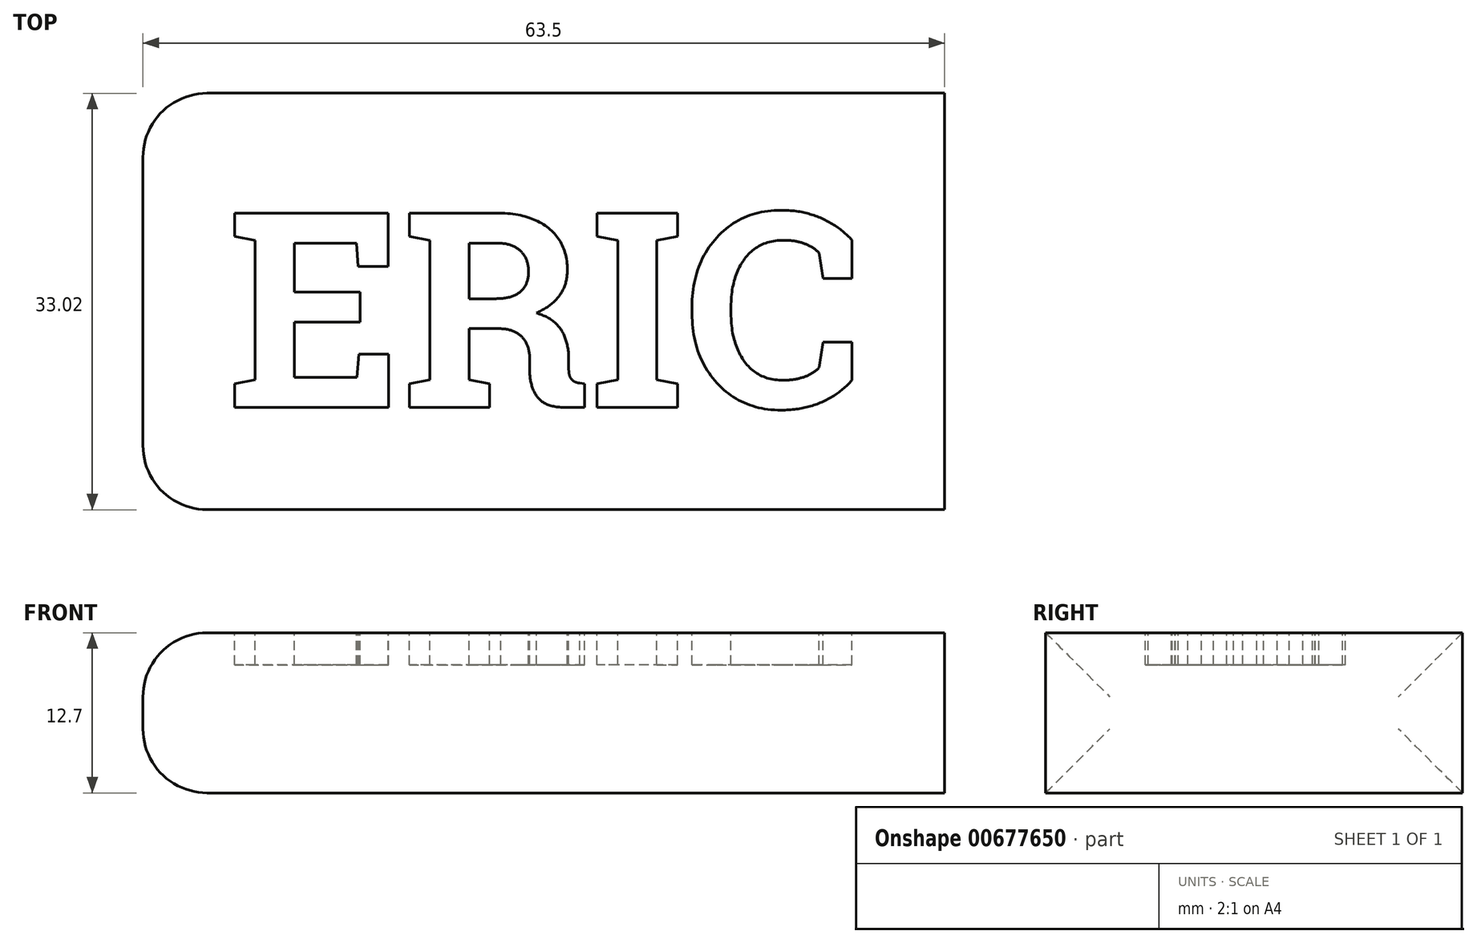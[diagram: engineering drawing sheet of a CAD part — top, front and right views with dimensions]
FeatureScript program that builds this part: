
annotation { "Feature Type Name" : "Feature", "Feature Type Description" : "" }
export const myFeature = defineFeature(function(context is Context, id is Id, definition is map)
    precondition{}
    {
        {
            var Q0;
            Q0=qCreatedBy(makeId("Top.planeOp"),FACE);
            var sketch = newSketch(context, id + "F0", { "sketchPlane" : qUnion([Q0])});
            skLineSegment(sketch, "E0.bottom", {"start": v(-31.03, 8.71) * mm, "end": v(32.47, 8.71) * mm});
            skLineSegment(sketch, "E0.top", {"start": v(-31.03, -24.3) * mm, "end": v(32.47, -24.3) * mm});
            skLineSegment(sketch, "E0.left", {"start": v(-31.03, 8.71) * mm, "end": v(-31.03, -24.3) * mm});
            skLineSegment(sketch, "E0.right", {"start": v(32.47, 8.71) * mm, "end": v(32.47, -24.3) * mm});
            skSolve(sketch);
        }
        {
            var Q0;
            Q0 = qSketchRegion(id + "F0", true);
            extrude(context, id + "F1", {"entities" : qUnion([Q0]), "depth" : 12.7 * mm, "offsetDistance" : 25.4 * mm});
        }
        {
            var Q0;
            Q0=makeQuery(id+"F1.opExtrude","CAP_FACE",FACE,{"disambiguationData":[OSD([sQuery(id+"F0.wireOp",EDGE,"E0.bottom"),sQuery(id+"F0.wireOp",EDGE,"E0.top"),sQuery(id+"F0.wireOp",EDGE,"E0.left"),sQuery(id+"F0.wireOp",EDGE,"E0.right")])],"isStart":false});
            var sketch = newSketch(context, id + "F2", { "sketchPlane" : qUnion([Q0])});
            skText(sketch, "E1", { "text": "ERIC", "fontName": "RobotoSlab-Bold.ttf"});
            const initialGuessF2  = {"E1": [-0.02437, -0.01619, 1, 0, 0.0156]};
            skSetInitialGuess(sketch, initialGuessF2);
            skSolve(sketch);
        }
        {
            var Q0;
            Q0 = qSketchRegion(id + "F2", true);
            extrude(context, id + "F3", {"entities" : qUnion([Q0]), "operationType" : NewBodyOperationType.REMOVE, "oppositeDirection" : true, "depth" : 2.54 * mm, "offsetDistance" : 25.4 * mm});
        }
        {
            var Q0;
            Q0=makeQuery(id+"F1.opExtrude","SWEPT_FACE",FACE,{"disambiguationData":[OSD([sQuery(id+"F0.wireOp",EDGE,"E0.left")])]});
            fillet(context, id + "F4", {"entities" : qUnion([Q0]), "radius" : 5.08 * mm, "tangentPropagation" : true, "allowEdgeOverflow" : false});
        }
    });
